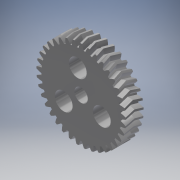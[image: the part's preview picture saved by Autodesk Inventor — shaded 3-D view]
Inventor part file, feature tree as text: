
AUTODESK INVENTOR PART (.ipt)
format: ipt  version: 2019 (Build 230136000, 136)  size: 918,016 bytes
history: native  units: mm (DEFAULTED — no unit token found)
features: sketch x4, plane x3, other x3, extrude x2, mirror x1, hole x1
ambient origin geometry x8: Origin, YZ Plane, XZ Plane, XY Plane, X Axis, Y Axis, Z Axis, Center Point
bodies: Solid1 (feature_tree)
feature tree (14):
  extrude  "Extrusion1"  Depth=5.0mm TaperAngle=0.0deg
  plane  "Work Plane2"
  plane  "Work Plane8"
  plane  "Work Plane9"
  other  "Spur Gear"
  mirror  "Mirror1"
  extrude  "Extrusion4"  Depth=10.0mm TaperAngle=0.0deg
  hole  "Hole2"  [1 undecoded]
  sketch  "Sketch1"  dims[d0=50.240958mm d1=5.0mm d2=0.0mm]
  sketch  "Sketch2"  dims[d3=47.741935mm d4=10.0mm d5=0.0mm]
  other  "Srf1"
  sketch  "Sketch6"  dims[d16=40.0mm d17=0.0mm d34=0.849079mm]
  sketch  "Sketch7"  dims[d39=0.0mm d41=0.0mm d43=40.0mm d46=40.0mm d47=0.0mm d48=0.0mm d66=7.5mm d67=5.0mm d68=0.0mm d69=25.0mm d70=30.0mm d72=360.0deg d74=5.0mm d75=6.0mm d76=10.0mm d77=7.0mm d78=90.0deg d79=10.0mm d80=0.0mm]
  other  "Pitch Diameter"
note: 1 required parameter value undecoded (feature->parameter linkage not recoverable at this tier; creation-order binding heuristic only, values carry confidence <= 0.55)
